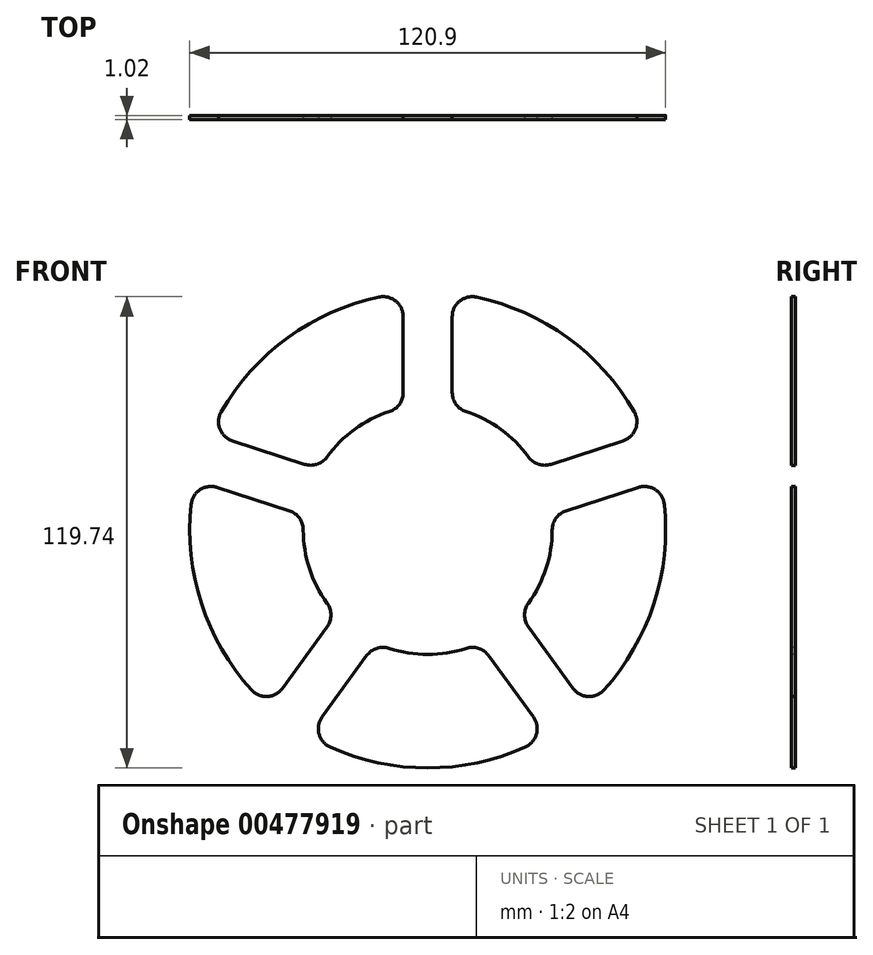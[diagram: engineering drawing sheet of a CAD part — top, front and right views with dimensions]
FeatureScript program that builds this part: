
annotation { "Feature Type Name" : "Feature", "Feature Type Description" : "" }
export const myFeature = defineFeature(function(context is Context, id is Id, definition is map)
    precondition{}
    {
        {
            var Q0;
            Q0=qCreatedBy(makeId("Front.planeOp"),FACE);
            var sketch = newSketch(context, id + "F0", { "sketchPlane" : qUnion([Q0])});
            skCircle(sketch, "E0", {"center": v(0, 0) * mm, "radius": 83 * mm});
            skCircle(sketch, "E1", {"center": v(0, 0) * mm, "radius": 20.64 * mm});
            skCircle(sketch, "E2", {"center": v(0, 69.85) * mm, "radius": 3.18 * mm});
            skCircle(sketch, "E3.1.0", {"center": v(-41.06, 56.5) * mm, "radius": 3.18 * mm});
            skCircle(sketch, "E3.2.0", {"center": v(-66.43, 21.58) * mm, "radius": 3.18 * mm});
            skCircle(sketch, "E3.3.0", {"center": v(-66.43, -21.58) * mm, "radius": 3.18 * mm});
            skCircle(sketch, "E3.4.0", {"center": v(-41.06, -56.5) * mm, "radius": 3.18 * mm});
            skCircle(sketch, "E3.5.0", {"center": v(0, -69.85) * mm, "radius": 3.18 * mm});
            skCircle(sketch, "E3.6.0", {"center": v(41.06, -56.5) * mm, "radius": 3.18 * mm});
            skCircle(sketch, "E3.7.0", {"center": v(66.43, -21.58) * mm, "radius": 3.18 * mm});
            skCircle(sketch, "E3.8.0", {"center": v(66.43, 21.58) * mm, "radius": 3.18 * mm});
            skCircle(sketch, "E3.9.0", {"center": v(41.06, 56.5) * mm, "radius": 3.18 * mm});
            skSolve(sketch);
        }
        {
            var Q0;
            Q0=makeQuery(id+"F0.imprint","IMPRINT",FACE,{"disambiguationData":[TD([[makeQuery(id+"F0.imprint","IMPRINT",EDGE,{"derivedFrom":sQuery(id+"F0.wireOp",EDGE,"E0")}),1.0]])]});
            extrude(context, id + "F1", {"entities" : qUnion([Q0]), "depth" : 1.02 * mm});
        }
        {
            var Q0;
            Q0=makeQuery(id+"F1.opExtrude","CAP_FACE",FACE,{"disambiguationData":[OSD([sQuery(id+"F0.wireOp",EDGE,"E0"),sQuery(id+"F0.wireOp",EDGE,"E1"),sQuery(id+"F0.wireOp",EDGE,"E2"),sQuery(id+"F0.wireOp",EDGE,"E3.1.0"),sQuery(id+"F0.wireOp",EDGE,"E3.2.0"),sQuery(id+"F0.wireOp",EDGE,"E3.3.0"),sQuery(id+"F0.wireOp",EDGE,"E3.4.0"),sQuery(id+"F0.wireOp",EDGE,"E3.5.0"),sQuery(id+"F0.wireOp",EDGE,"E3.6.0"),sQuery(id+"F0.wireOp",EDGE,"E3.7.0"),sQuery(id+"F0.wireOp",EDGE,"E3.8.0"),sQuery(id+"F0.wireOp",EDGE,"E3.9.0")])],"isStart":false});
            var sketch = newSketch(context, id + "F2", { "sketchPlane" : qUnion([Q0])});
            skLineSegment(sketch, "E4", {"start": v(0, 0) * mm, "end": v(0, 63.06) * mm, "construction": true});
            skLineSegment(sketch, "E5", {"start": v(0, 0) * mm, "end": v(-66.43, 21.58) * mm, "construction": true});
            skArc(sketch, "E6", {"start": v(-52.47, 30.02) * mm, "mid": v(-35.53, 48.9) * mm, "end": v(-12.34, 59.18) * mm});
            skArc(sketch, "E7", {"start": v(-25.6, 18.56) * mm, "mid": v(-18.59, 25.58) * mm, "end": v(-9.74, 30.09) * mm});
            skLineSegment(sketch, "E8.trimOffspring", {"start": v(-31.29, 16.7) * mm, "end": v(-49.63, 22.67) * mm});
            skLineSegment(sketch, "E9.trimOffspring", {"start": v(-6.22, 34.92) * mm, "end": v(-6.22, 54.2) * mm});
            skPoint(sketch, "E10.visualSharp", {"position": v(-55.26, 24.5) * mm});
            skArc(sketch, "E10.filletArc", {"start": v(-52.47, 30.02) * mm, "mid": v(-52.8, 25.67) * mm, "end": v(-49.63, 22.67) * mm});
            skPoint(sketch, "E11.visualSharp", {"position": v(-6.22, 60.13) * mm});
            skArc(sketch, "E11.filletArc", {"start": v(-6.22, 54.2) * mm, "mid": v(-8.1, 58.15) * mm, "end": v(-12.34, 59.18) * mm});
            skPoint(sketch, "E12.visualSharp", {"position": v(-6.22, 31) * mm});
            skArc(sketch, "E12.filletArc", {"start": v(-9.74, 30.09) * mm, "mid": v(-7.2, 31.93) * mm, "end": v(-6.22, 34.92) * mm});
            skPoint(sketch, "E13.visualSharp", {"position": v(-27.56, 15.5) * mm});
            skArc(sketch, "E13.filletArc", {"start": v(-31.29, 16.7) * mm, "mid": v(-28.14, 16.7) * mm, "end": v(-25.6, 18.56) * mm});
            skArc(sketch, "E14.1.0", {"start": v(-44.77, -40.62) * mm, "mid": v(-57.5, -18.68) * mm, "end": v(-60.1, 6.55) * mm});
            skArc(sketch, "E14.1.1", {"start": v(-53.48, 10.83) * mm, "mid": v(-57.8, 10.27) * mm, "end": v(-60.1, 6.55) * mm});
            skLineSegment(sketch, "E14.1.2", {"start": v(-35.13, 4.87) * mm, "end": v(-53.48, 10.83) * mm});
            skArc(sketch, "E14.1.3", {"start": v(-31.62, 0.04) * mm, "mid": v(-32.6, 3.02) * mm, "end": v(-35.13, 4.87) * mm});
            skArc(sketch, "E14.1.4", {"start": v(-25.56, -18.62) * mm, "mid": v(-30.08, -9.77) * mm, "end": v(-31.62, 0.04) * mm});
            skArc(sketch, "E14.1.5", {"start": v(-25.56, -24.6) * mm, "mid": v(-24.59, -21.6) * mm, "end": v(-25.56, -18.62) * mm});
            skLineSegment(sketch, "E14.1.6", {"start": v(-25.56, -24.6) * mm, "end": v(-36.9, -40.2) * mm});
            skArc(sketch, "E14.1.7", {"start": v(-44.77, -40.62) * mm, "mid": v(-40.73, -42.28) * mm, "end": v(-36.9, -40.2) * mm});
            skArc(sketch, "E14.2.0", {"start": v(24.8, -55.13) * mm, "mid": v(0, -60.45) * mm, "end": v(-24.8, -55.13) * mm});
            skArc(sketch, "E14.2.1", {"start": v(-26.83, -47.51) * mm, "mid": v(-27.63, -51.8) * mm, "end": v(-24.8, -55.13) * mm});
            skLineSegment(sketch, "E14.2.2", {"start": v(-15.5, -31.9) * mm, "end": v(-26.83, -47.51) * mm});
            skArc(sketch, "E14.2.3", {"start": v(-9.8, -30.06) * mm, "mid": v(-12.95, -30.06) * mm, "end": v(-15.5, -31.9) * mm});
            skArc(sketch, "E14.2.4", {"start": v(9.8, -30.06) * mm, "mid": v(0, -31.62) * mm, "end": v(-9.8, -30.06) * mm});
            skArc(sketch, "E14.2.5", {"start": v(15.5, -31.9) * mm, "mid": v(12.95, -30.06) * mm, "end": v(9.8, -30.06) * mm});
            skLineSegment(sketch, "E14.2.6", {"start": v(15.5, -31.9) * mm, "end": v(26.83, -47.51) * mm});
            skArc(sketch, "E14.2.7", {"start": v(24.8, -55.13) * mm, "mid": v(27.63, -51.8) * mm, "end": v(26.83, -47.51) * mm});
            skArc(sketch, "E14.3.0", {"start": v(60.1, 6.55) * mm, "mid": v(57.5, -18.68) * mm, "end": v(44.77, -40.62) * mm});
            skArc(sketch, "E14.3.1", {"start": v(36.9, -40.2) * mm, "mid": v(40.73, -42.28) * mm, "end": v(44.77, -40.62) * mm});
            skLineSegment(sketch, "E14.3.2", {"start": v(25.56, -24.6) * mm, "end": v(36.9, -40.2) * mm});
            skArc(sketch, "E14.3.3", {"start": v(25.56, -18.62) * mm, "mid": v(24.59, -21.6) * mm, "end": v(25.56, -24.6) * mm});
            skArc(sketch, "E14.3.4", {"start": v(31.62, 0.04) * mm, "mid": v(30.08, -9.77) * mm, "end": v(25.56, -18.62) * mm});
            skArc(sketch, "E14.3.5", {"start": v(35.13, 4.87) * mm, "mid": v(32.6, 3.02) * mm, "end": v(31.62, 0.04) * mm});
            skLineSegment(sketch, "E14.3.6", {"start": v(35.13, 4.87) * mm, "end": v(53.48, 10.83) * mm});
            skArc(sketch, "E14.3.7", {"start": v(60.1, 6.55) * mm, "mid": v(57.8, 10.27) * mm, "end": v(53.48, 10.83) * mm});
            skArc(sketch, "E14.4.0", {"start": v(12.34, 59.18) * mm, "mid": v(35.53, 48.9) * mm, "end": v(52.47, 30.02) * mm});
            skArc(sketch, "E14.4.1", {"start": v(49.63, 22.67) * mm, "mid": v(52.8, 25.67) * mm, "end": v(52.47, 30.02) * mm});
            skLineSegment(sketch, "E14.4.2", {"start": v(31.29, 16.7) * mm, "end": v(49.63, 22.67) * mm});
            skArc(sketch, "E14.4.3", {"start": v(25.6, 18.56) * mm, "mid": v(28.14, 16.7) * mm, "end": v(31.29, 16.7) * mm});
            skArc(sketch, "E14.4.4", {"start": v(9.74, 30.09) * mm, "mid": v(18.59, 25.58) * mm, "end": v(25.6, 18.56) * mm});
            skArc(sketch, "E14.4.5", {"start": v(6.22, 34.92) * mm, "mid": v(7.2, 31.93) * mm, "end": v(9.74, 30.09) * mm});
            skLineSegment(sketch, "E14.4.6", {"start": v(6.22, 34.92) * mm, "end": v(6.22, 54.2) * mm});
            skArc(sketch, "E14.4.7", {"start": v(12.34, 59.18) * mm, "mid": v(8.1, 58.15) * mm, "end": v(6.22, 54.2) * mm});
            skSolve(sketch);
        }
        {
            var Q0;
            Q0=makeQuery(id+"F2.imprint","IMPRINT",FACE,{"disambiguationData":[TD([[makeQuery(id+"F2.imprint","IMPRINT",EDGE,{"derivedFrom":sQuery(id+"F2.wireOp",EDGE,"E6")}),-1.0]])]});
            var Q1;
            Q1=makeQuery(id+"F2.imprint","IMPRINT",FACE,{"disambiguationData":[TD([[makeQuery(id+"F2.imprint","IMPRINT",EDGE,{"derivedFrom":sQuery(id+"F2.wireOp",EDGE,"E14.1.0")}),-1.0]])]});
            var Q2;
            Q2=makeQuery(id+"F2.imprint","IMPRINT",FACE,{"disambiguationData":[TD([[makeQuery(id+"F2.imprint","IMPRINT",EDGE,{"derivedFrom":sQuery(id+"F2.wireOp",EDGE,"E14.2.0")}),-1.0]])]});
            var Q3;
            Q3=makeQuery(id+"F2.imprint","IMPRINT",FACE,{"disambiguationData":[TD([[makeQuery(id+"F2.imprint","IMPRINT",EDGE,{"derivedFrom":sQuery(id+"F2.wireOp",EDGE,"E14.4.0")}),-1.0]])]});
            var Q4;
            Q4=makeQuery(id+"F2.imprint","IMPRINT",FACE,{"disambiguationData":[TD([[makeQuery(id+"F2.imprint","IMPRINT",EDGE,{"derivedFrom":sQuery(id+"F2.wireOp",EDGE,"E14.3.0")}),-1.0]])]});
            extrude(context, id + "F3", {"entities" : qUnion([Q0, Q1, Q2, Q3, Q4]), "operationType" : NewBodyOperationType.REMOVE, "endBound" : BoundingType.THROUGH_ALL, "oppositeDirection" : true, "depth" : 25.4 * mm});
        }
    });
